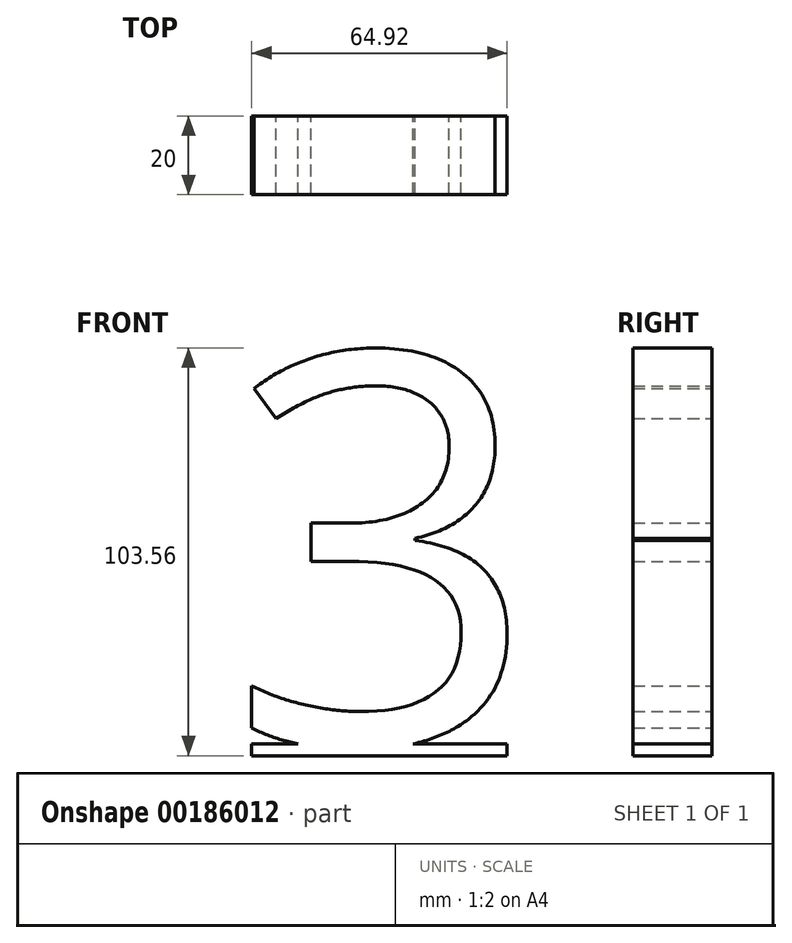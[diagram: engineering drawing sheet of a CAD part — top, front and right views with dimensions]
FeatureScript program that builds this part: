
annotation { "Feature Type Name" : "Feature", "Feature Type Description" : "" }
export const myFeature = defineFeature(function(context is Context, id is Id, definition is map)
    precondition{}
    {
        {
            var Q0;
            Q0=qCreatedBy(makeId("Front.planeOp"),FACE);
            var sketch = newSketch(context, id + "F0", { "sketchPlane" : qUnion([Q0])});
            skText(sketch, "E0", { "text": "3", "fontName": "OpenSans-Regular.ttf"});
            const initialGuessF0  = {"E0": [-0.04014, 0, 1, 0, 0.1]};
            skSetInitialGuess(sketch, initialGuessF0);
            skSolve(sketch);
        }
        {
            var Q0;
            Q0=makeQuery(id+"F0.imprint","IMPRINT",FACE,{"disambiguationData":[TD([[makeQuery(id+"F0.imprint","IMPRINT",EDGE,{"derivedFrom":sQuery(id+"F0.wireOp",EDGE,"E0.sketch_text.stroke-0")}),-1.0]])]});
            extrude(context, id + "F1", {"entities" : qUnion([Q0]), "depth" : 10 * mm, "hasSecondDirection" : true, "secondDirectionOppositeDirection" : true, "secondDirectionDepth" : 10 * mm});
        }
        {
            var Q0;
            Q0=qCreatedBy(makeId("Top.planeOp"),FACE);
            var sketch = newSketch(context, id + "F2", { "sketchPlane" : qUnion([Q0])});
            skLineSegment(sketch, "E1.bottom", {"start": v(-33.78, 10) * mm, "end": v(31.14, 10) * mm});
            skLineSegment(sketch, "E1.top", {"start": v(-33.78, -10) * mm, "end": v(31.14, -10) * mm});
            skLineSegment(sketch, "E1.left", {"start": v(31.14, 10) * mm, "end": v(31.14, -10) * mm});
            skLineSegment(sketch, "E1.right", {"start": v(-33.78, 10) * mm, "end": v(-33.78, -10) * mm});
            skSolve(sketch);
        }
        {
            var Q0;
            Q0=qSketchRegion(id+"F2",true);
            extrude(context, id + "F3", {"entities" : qUnion([Q0]), "operationType" : NewBodyOperationType.ADD, "oppositeDirection" : true, "depth" : 3 * mm});
        }
    });
